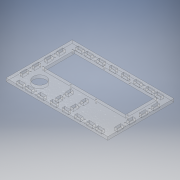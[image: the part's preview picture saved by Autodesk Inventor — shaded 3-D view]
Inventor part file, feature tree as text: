
AUTODESK INVENTOR PART (.ipt)
format: ipt  version: 2019 (Build 230136000, 136)  size: 309,760 bytes
history: native  units: mm
features: extrude x1, sketch x1
ambient origin geometry x8: Origin, YZ Plane, XZ Plane, XY Plane, X Axis, Y Axis, Z Axis, Center Point
bodies: Body1 (feature_tree)
feature tree (2):
  extrude  "Extrusion3"  Depth=200.0mm
  sketch  "Sketch1"  dims[d0=130.0mm d1=200.0mm d31=5.1mm d32=4.45mm d34=6.15mm d35=11.7mm d36=12.3mm d37=11.7mm d38=6.15mm d39=11.7mm d40=12.3mm d41=11.7mm d42=12.3mm d43=11.7mm d44=6.3mm d45=11.7mm d46=5.1mm d47=4.45mm d48=6.0mm d49=0.0mm d58=160.0mm d59=60.0mm d60=15.0mm d61=20.0mm d66=25.0mm d67=20.0mm d78=2.25mm d80=3.0mm d81=3.0mm d82=3.0mm d83=25.0mm d84=2.55mm d85=6.15mm d86=2.55mm d87=6.15mm d88=5.1mm d89=9.7mm d90=20.0mm d92=29.9mm d93=20.0mm d95=20.0mm d98=5.0mm d99=2.25mm d100=5.15mm d101=2.55mm d102=27.0mm]
